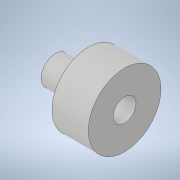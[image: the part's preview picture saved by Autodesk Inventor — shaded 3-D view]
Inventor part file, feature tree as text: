
AUTODESK INVENTOR PART (.ipt)
format: ipt  version: 2021 (Build 250183000, 183)  size: 114,176 bytes
history: native  units: in
note: dims shown in document units (in); Inventor stores cm internally (conversion verified against a paired STEP export)
features: extrude x2, sketch x2, chamfer x1
ambient origin geometry x8: Origin, YZ Plane, XZ Plane, XY Plane, X Axis, Y Axis, Z Axis, Center Point
bodies: Solid1 (feature_tree)
feature tree (5):
  extrude  "Extrusion1"  Depth=0.315in
  extrude  "Extrusion2"  Depth=0.5in
  chamfer  "Chamfer2"  Distance=0.5in
  sketch  "Sketch1"  dims[d0=0.394in d1=0.315in]
  sketch  "Sketch2"  dims[d2=0.453in d3=0.0in d4=1.0in d5=0.5in d6=0.0in d7=0.315in d12=0.01in d13=0.125in d14=45.0deg d15=0.0344in]
